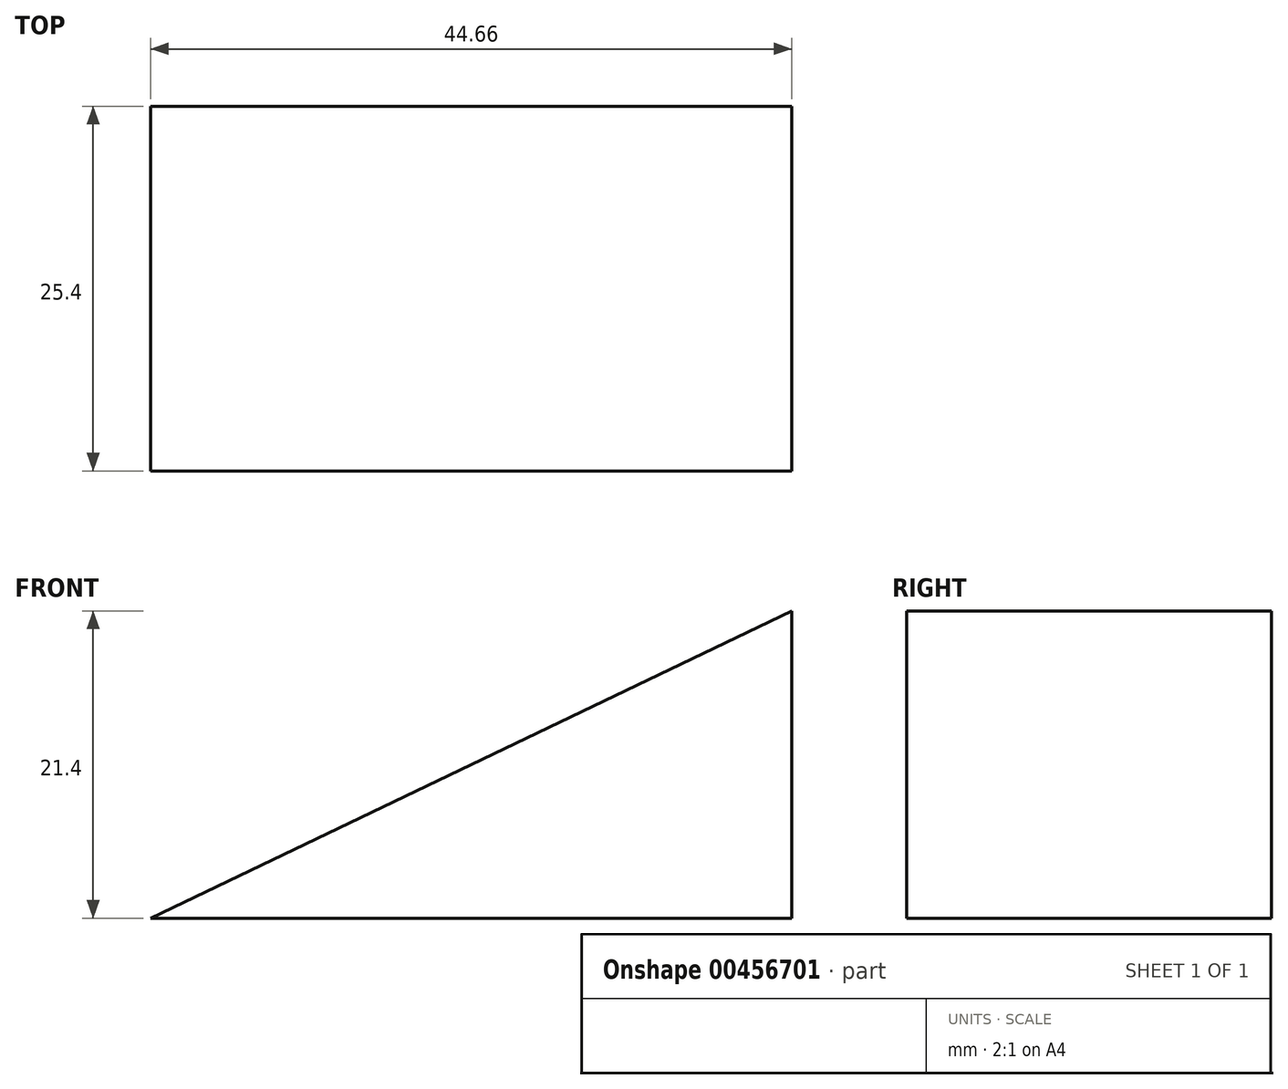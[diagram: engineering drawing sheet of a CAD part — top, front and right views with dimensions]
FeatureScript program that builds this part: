
annotation { "Feature Type Name" : "Feature", "Feature Type Description" : "" }
export const myFeature = defineFeature(function(context is Context, id is Id, definition is map)
    precondition{}
    {
        {
            var Q0;
            Q0=qCreatedBy(makeId("Front.planeOp"),FACE);
            var sketch = newSketch(context, id + "F0", { "sketchPlane" : qUnion([Q0])});
            skLineSegment(sketch, "E0", {"start": v(0, 0) * mm, "end": v(44.66, 0) * mm});
            skLineSegment(sketch, "E1", {"start": v(44.66, 0) * mm, "end": v(44.66, 21.4) * mm});
            skLineSegment(sketch, "E2", {"start": v(44.66, 21.4) * mm, "end": v(0, 0) * mm});
            skSolve(sketch);
        }
        {
            var Q0;
            Q0=makeQuery(id+"F0.imprint","IMPRINT",FACE,{"disambiguationData":[TD([[makeQuery(id+"F0.imprint","IMPRINT",EDGE,{"derivedFrom":sQuery(id+"F0.wireOp",EDGE,"E0")}),1.0]])]});
            extrude(context, id + "F1", {"entities" : qUnion([Q0]), "depth" : 25.4 * mm});
        }
    });
